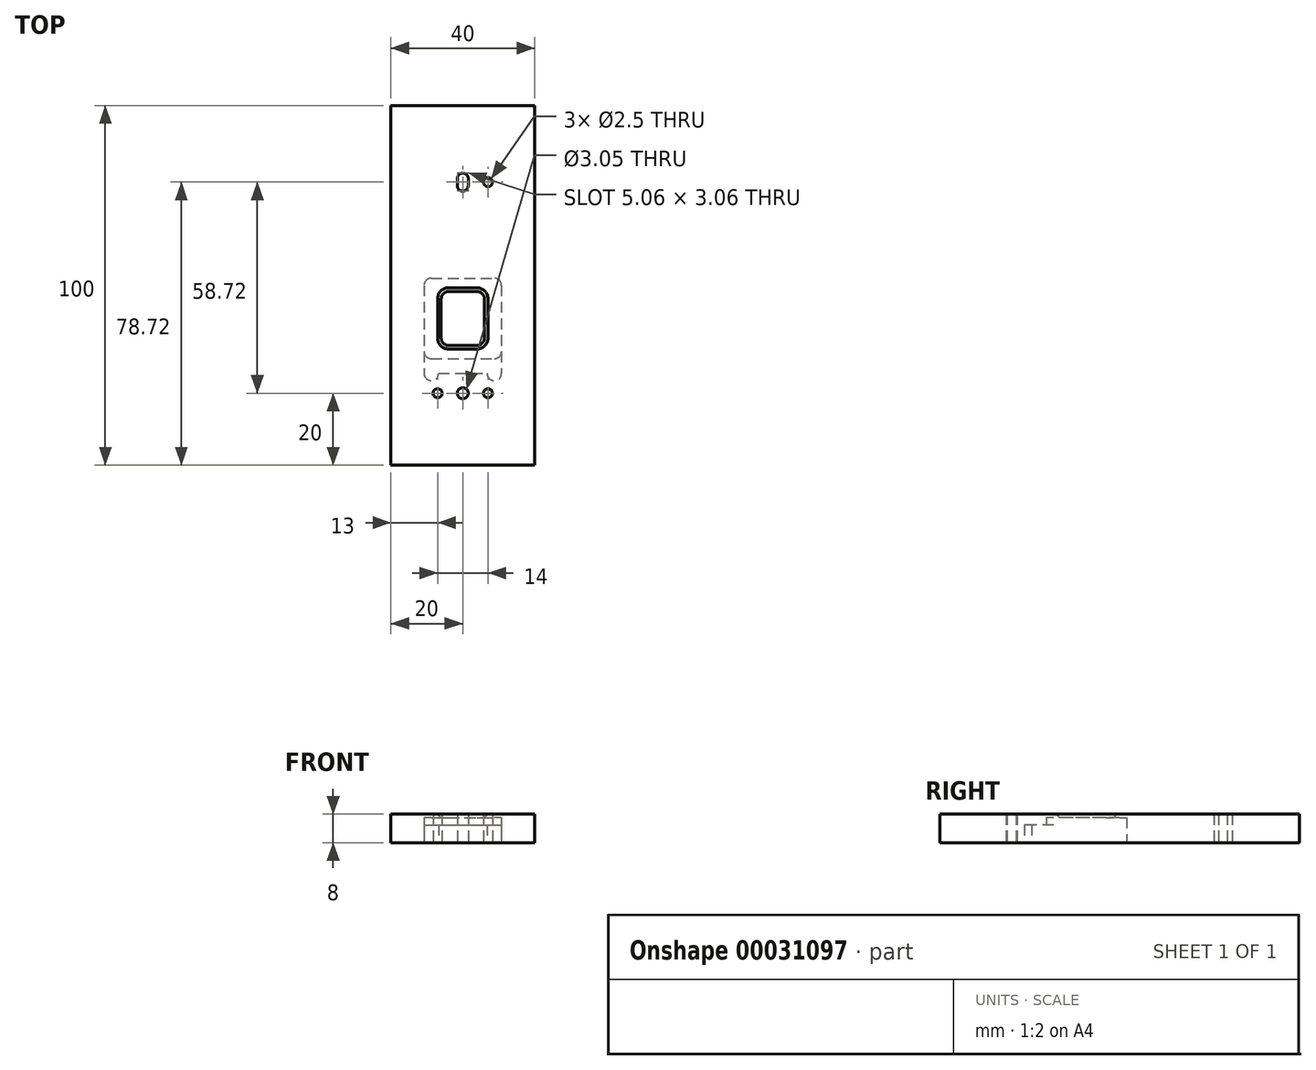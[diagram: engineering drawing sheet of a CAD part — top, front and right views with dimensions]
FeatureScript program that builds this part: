
annotation { "Feature Type Name" : "Feature", "Feature Type Description" : "" }
export const myFeature = defineFeature(function(context is Context, id is Id, definition is map)
    precondition{}
    {
        {
            var Q0;
            Q0=qCreatedBy(makeId("Top.planeOp"),FACE);
            var sketch = newSketch(context, id + "F0", { "sketchPlane" : qUnion([Q0])});
            skCircle(sketch, "E0", {"center": v(0, 0) * mm, "radius": 1.52 * mm});
            skCircle(sketch, "E1", {"center": v(-7, 0) * mm, "radius": 1.25 * mm});
            skCircle(sketch, "E2", {"center": v(7, 0) * mm, "radius": 1.25 * mm});
            skLineSegment(sketch, "E3", {"start": v(-7, 0) * mm, "end": v(7, 0) * mm, "construction": true});
            skLineSegment(sketch, "E4", {"start": v(0, 0) * mm, "end": v(0, 58.72) * mm, "construction": true});
            skLineSegment(sketch, "E5", {"start": v(0, 58.72) * mm, "end": v(7, 58.72) * mm, "construction": true});
            skLineSegment(sketch, "E6.bottom", {"start": v(-4, 28.3) * mm, "end": v(4, 28.3) * mm});
            skLineSegment(sketch, "E6.top", {"start": v(-4, 13.3) * mm, "end": v(4, 13.3) * mm});
            skLineSegment(sketch, "E6.left", {"start": v(-6, 26.3) * mm, "end": v(-6, 15.3) * mm});
            skLineSegment(sketch, "E6.right", {"start": v(6, 26.3) * mm, "end": v(6, 15.3) * mm});
            skLineSegment(sketch, "E7.bottom", {"start": v(-8.75, 32) * mm, "end": v(8.75, 32) * mm});
            skLineSegment(sketch, "E7.top", {"start": v(-6.75, 5.5) * mm, "end": v(6.75, 5.5) * mm});
            skLineSegment(sketch, "E7.left", {"start": v(-10.75, 30) * mm, "end": v(-10.75, 11.6) * mm});
            skLineSegment(sketch, "E7.right", {"start": v(10.75, 30) * mm, "end": v(10.75, 11.6) * mm});
            skArc(sketch, "E8", {"start": v(-10.75, 5.5) * mm, "mid": v(-8.75, 3.5) * mm, "end": v(-6.75, 5.5) * mm});
            skArc(sketch, "E9", {"start": v(6.75, 5.5) * mm, "mid": v(8.75, 3.5) * mm, "end": v(10.75, 5.5) * mm});
            skPoint(sketch, "E10", {"position": v(0, 5.5) * mm});
            skPoint(sketch, "E11", {"position": v(0, 13.3) * mm});
            skPoint(sketch, "E12.visualSharp", {"position": v(-10.75, 32) * mm});
            skArc(sketch, "E12.filletArc", {"start": v(-8.75, 32) * mm, "mid": v(-10.16, 31.41) * mm, "end": v(-10.75, 30) * mm});
            skPoint(sketch, "E13.visualSharp", {"position": v(10.75, 32) * mm});
            skArc(sketch, "E13.filletArc", {"start": v(10.75, 30) * mm, "mid": v(10.16, 31.41) * mm, "end": v(8.75, 32) * mm});
            skPoint(sketch, "E14.visualSharp", {"position": v(6, 13.3) * mm});
            skArc(sketch, "E14.filletArc", {"start": v(4, 13.3) * mm, "mid": v(5.41, 13.89) * mm, "end": v(6, 15.3) * mm});
            skPoint(sketch, "E15.visualSharp", {"position": v(-6, 13.3) * mm});
            skArc(sketch, "E15.filletArc", {"start": v(-6, 15.3) * mm, "mid": v(-5.41, 13.89) * mm, "end": v(-4, 13.3) * mm});
            skPoint(sketch, "E16.visualSharp", {"position": v(-6, 28.3) * mm});
            skArc(sketch, "E16.filletArc", {"start": v(-4, 28.3) * mm, "mid": v(-5.41, 27.71) * mm, "end": v(-6, 26.3) * mm});
            skPoint(sketch, "E17.visualSharp", {"position": v(6, 28.3) * mm});
            skArc(sketch, "E17.filletArc", {"start": v(6, 26.3) * mm, "mid": v(5.41, 27.71) * mm, "end": v(4, 28.3) * mm});
            skLineSegment(sketch, "E18", {"start": v(-8.75, 9.6) * mm, "end": v(8.75, 9.6) * mm});
            skCircle(sketch, "E19", {"center": v(7, 58.72) * mm, "radius": 1.25 * mm});
            skLineSegment(sketch, "E20", {"start": v(0, 59.72) * mm, "end": v(0, 57.72) * mm, "construction": true});
            skPoint(sketch, "E21", {"position": v(0, 58.72) * mm});
            skArc(sketch, "E22.0.startCap", {"start": v(-1.53, 59.72) * mm, "mid": v(0, 61.25) * mm, "end": v(1.53, 59.72) * mm});
            skArc(sketch, "E22.0.endCap", {"start": v(1.53, 57.72) * mm, "mid": v(0, 56.2) * mm, "end": v(-1.53, 57.72) * mm});
            skLineSegment(sketch, "E22.0.left", {"start": v(1.53, 59.72) * mm, "end": v(1.53, 57.72) * mm});
            skLineSegment(sketch, "E22.0.right", {"start": v(-1.53, 59.72) * mm, "end": v(-1.53, 57.72) * mm});
            skLineSegment(sketch, "E23.bottom", {"start": v(-20, 80) * mm, "end": v(20, 80) * mm});
            skLineSegment(sketch, "E23.top", {"start": v(-20, -20) * mm, "end": v(20, -20) * mm});
            skLineSegment(sketch, "E23.left", {"start": v(-20, 80) * mm, "end": v(-20, -20) * mm});
            skLineSegment(sketch, "E23.right", {"start": v(20, 80) * mm, "end": v(20, -20) * mm});
            skPoint(sketch, "E24", {"position": v(0, -20) * mm});
            skArc(sketch, "E25.filletArc", {"start": v(-10.75, 11.6) * mm, "mid": v(-10.16, 10.19) * mm, "end": v(-8.75, 9.6) * mm});
            skArc(sketch, "E26.filletArc", {"start": v(8.75, 9.6) * mm, "mid": v(10.16, 10.19) * mm, "end": v(10.75, 11.6) * mm});
            skLineSegment(sketch, "E27", {"start": v(-10.75, 11.6) * mm, "end": v(-10.75, 5.5) * mm});
            skLineSegment(sketch, "E28", {"start": v(10.75, 11.6) * mm, "end": v(10.75, 5.5) * mm});
            skSolve(sketch);
        }
        {
            var Q0;
            Q0=makeQuery(id+"F0.imprint","IMPRINT",FACE,{"disambiguationData":[TD([[makeQuery(id+"F0.imprint","IMPRINT",EDGE,{"derivedFrom":sQuery(id+"F0.wireOp",EDGE,"E0")}),-1.0]])]});
            var Q1;
            Q1=makeQuery(id+"F0.imprint","IMPRINT",FACE,{"disambiguationData":[TD([[makeQuery(id+"F0.imprint","IMPRINT",EDGE,{"derivedFrom":sQuery(id+"F0.wireOp",EDGE,"E6.bottom")}),1.0]])]});
            var Q2;
            Q2=makeQuery(id+"F0.imprint","IMPRINT",FACE,{"disambiguationData":[TD([[makeQuery(id+"F0.imprint","IMPRINT",EDGE,{"derivedFrom":sQuery(id+"F0.wireOp",EDGE,"E7.top")}),1.0]])]});
            var Q3;
            Q3=sQuery(id+"F0.wireOp",EDGE,"E23.bottom");
            var Q4;
            Q4=sQuery(id+"F0.wireOp",EDGE,"E23.left");
            var Q5;
            Q5=sQuery(id+"F0.wireOp",EDGE,"E23.right");
            var Q6;
            Q6=sQuery(id+"F0.wireOp",EDGE,"E23.top");
            extrude(context, id + "F1", {"entities" : qUnion([Q0, Q1, Q2]), "surfaceEntities" : qUnion([Q3, Q4, Q5, Q6]), "depth" : 8 * mm});
        }
        {
            var Q0;
            Q0=makeQuery(id+"F0.imprint","IMPRINT",FACE,{"disambiguationData":[TD([[makeQuery(id+"F0.imprint","IMPRINT",EDGE,{"derivedFrom":sQuery(id+"F0.wireOp",EDGE,"E6.bottom")}),1.0]])]});
            extrude(context, id + "F2", {"entities" : qUnion([Q0]), "operationType" : NewBodyOperationType.REMOVE, "depth" : 7 * mm});
        }
        {
            var Q0;
            Q0=makeQuery(id+"F0.imprint","IMPRINT",FACE,{"disambiguationData":[TD([[makeQuery(id+"F0.imprint","IMPRINT",EDGE,{"derivedFrom":sQuery(id+"F0.wireOp",EDGE,"E7.top")}),1.0]])]});
            extrude(context, id + "F3", {"entities" : qUnion([Q0]), "operationType" : NewBodyOperationType.REMOVE, "depth" : 5 * mm});
        }
        {
            var Q0;
            Q0=makeQuery(id+"F1.opExtrude","CAP_EDGE",EDGE,{"disambiguationData":[OSD([sQuery(id+"F0.wireOp",EDGE,"E6.right")])],"isStart":false});
            var Q1;
            Q1=makeQuery(id+"F1.opExtrude","CAP_EDGE",EDGE,{"disambiguationData":[OSD([sQuery(id+"F0.wireOp",EDGE,"E14.filletArc")])],"isStart":false});
            var Q2;
            Q2=makeQuery(id+"F1.opExtrude","CAP_EDGE",EDGE,{"disambiguationData":[OSD([sQuery(id+"F0.wireOp",EDGE,"E6.top")])],"isStart":false});
            var Q3;
            Q3=makeQuery(id+"F1.opExtrude","CAP_EDGE",EDGE,{"disambiguationData":[OSD([sQuery(id+"F0.wireOp",EDGE,"E15.filletArc")])],"isStart":false});
            var Q4;
            Q4=makeQuery(id+"F1.opExtrude","CAP_EDGE",EDGE,{"disambiguationData":[OSD([sQuery(id+"F0.wireOp",EDGE,"E6.left")])],"isStart":false});
            var Q5;
            Q5=makeQuery(id+"F1.opExtrude","CAP_EDGE",EDGE,{"disambiguationData":[OSD([sQuery(id+"F0.wireOp",EDGE,"E16.filletArc")])],"isStart":false});
            var Q6;
            Q6=makeQuery(id+"F1.opExtrude","CAP_EDGE",EDGE,{"disambiguationData":[OSD([sQuery(id+"F0.wireOp",EDGE,"E6.bottom")])],"isStart":false});
            var Q7;
            Q7=makeQuery(id+"F1.opExtrude","CAP_EDGE",EDGE,{"disambiguationData":[OSD([sQuery(id+"F0.wireOp",EDGE,"E17.filletArc")])],"isStart":false});
            chamfer(context, id + "F4", {"entities" : qUnion([Q0, Q1, Q2, Q3, Q4, Q5, Q6, Q7]), "width" : 1 * mm, "tangentPropagation" : true});
        }
    });
